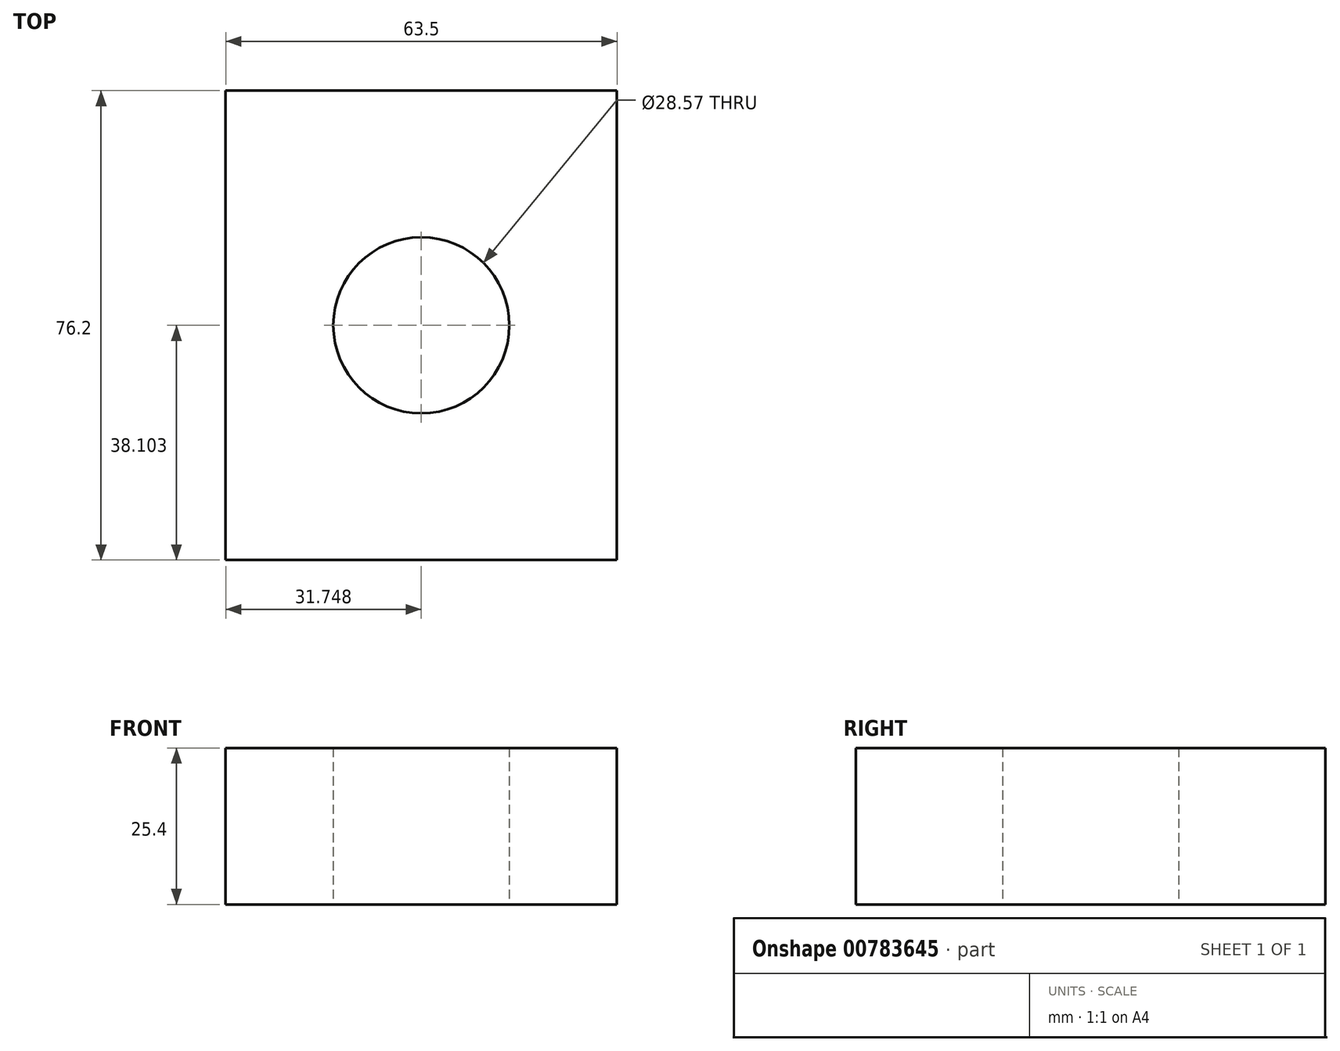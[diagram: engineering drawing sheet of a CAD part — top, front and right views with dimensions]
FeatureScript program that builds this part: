
annotation { "Feature Type Name" : "Feature", "Feature Type Description" : "" }
export const myFeature = defineFeature(function(context is Context, id is Id, definition is map)
    precondition{}
    {
        {
            var Q0;
            Q0=qCreatedBy(makeId("Top.planeOp"),FACE);
            var sketch = newSketch(context, id + "F0", { "sketchPlane" : qUnion([Q0])});
            skLineSegment(sketch, "E0", {"start": v(-61.1, 52.62) * mm, "end": v(-61.1, -23.58) * mm});
            skLineSegment(sketch, "E1", {"start": v(-61.1, -23.58) * mm, "end": v(2.4, -23.58) * mm});
            skLineSegment(sketch, "E2", {"start": v(-61.1, 52.62) * mm, "end": v(2.4, 52.62) * mm});
            skLineSegment(sketch, "E3", {"start": v(2.4, 52.62) * mm, "end": v(2.4, -23.58) * mm});
            skLineSegment(sketch, "E4", {"start": v(-61.1, -14.05) * mm, "end": v(2.4, -14.05) * mm});
            skLineSegment(sketch, "E5", {"start": v(-61.1, 43.1) * mm, "end": v(2.4, 43.1) * mm});
            skLineSegment(sketch, "E6", {"start": v(2.4, -23.58) * mm, "end": v(26.21, -23.58) * mm});
            skLineSegment(sketch, "E7", {"start": v(2.4, 52.62) * mm, "end": v(26.21, 52.62) * mm});
            skLineSegment(sketch, "E8", {"start": v(26.21, 52.62) * mm, "end": v(72.57, 20.24) * mm});
            skLineSegment(sketch, "E9", {"start": v(26.21, -23.58) * mm, "end": v(72.57, 10.72) * mm});
            skLineSegment(sketch, "E10", {"start": v(72.57, 20.24) * mm, "end": v(72.57, 10.72) * mm});
            skCircle(sketch, "E11", {"center": v(-29.35, 14.52) * mm, "radius": 14.29 * mm});
            skSolve(sketch);
        }
        {
            var Q0;
            {var subQ1=sQuery(id+"F0.wireOp",EDGE,"E4");Q0=makeQuery(id+"F0.imprint","IMPRINT",FACE,{"disambiguationData":[TD([[makeQuery(id+"F0.imprint","IMPRINT",EDGE,{"derivedFrom":subQ1}),1.0]])]});}
            var Q1;
            {var subQ0=sQuery(id+"F0.wireOp",EDGE,"E2");Q1=makeQuery(id+"F0.imprint","IMPRINT",FACE,{"disambiguationData":[TD([[makeQuery(id+"F0.imprint","IMPRINT",EDGE,{"derivedFrom":subQ0}),-1.0]])]});}
            var Q2;
            {var subQ0=sQuery(id+"F0.wireOp",EDGE,"E1");Q2=makeQuery(id+"F0.imprint","IMPRINT",FACE,{"disambiguationData":[TD([[makeQuery(id+"F0.imprint","IMPRINT",EDGE,{"derivedFrom":subQ0}),1.0]])]});}
            extrude(context, id + "F1", {"entities" : qUnion([Q0, Q1, Q2]), "depth" : 25.4 * mm, "offsetDistance" : 25.4 * mm});
        }
    });
